# Revit family: 206_HDW-_
name_source: partatom
category: Duct Accessories
units: mm (PartAtom-declared; Revit-internal decimal feet)

## family parameters
Always vertical = Yes
Cut with Voids When Loaded = No
Part Type = Breaks Into
Round Connector Dimension = Use Diameter
Shared = No
Work Plane-Based = No

## types (7) — shared parameters
CAT0 = Yes
Description = HEATING COIL FOR CIRCULAR DUCTING
Manufacturer = Alnor
QmdConnectorList = 201;D;202;D
URL = http://www.ventilation-alnor.co.uk
magiPartTypeId = 206
magiProductFamilyId = HDW-*

## per-type parameters (varying)
| type | CBB | CH | CHH | D | H2D | L2D | LL | W2D |
| HDW-100 | 108 mm | 190 mm  [stored 0.62336 ft] | 95 mm  [stored 0.31168 ft] | 100 mm | 190 mm  [stored 0.62336 ft] | 220 mm  [stored 0.721785 ft] | 110 mm  [stored 0.360892 ft] | 214 mm |
| HDW-315 | 230 mm | 440 mm | 220 mm  [stored 0.721785 ft] | 315 mm | 439 mm | 260 mm | 130 mm | 459 mm |
| HDW-250 | 198 mm | 365 mm | 183 mm | 250 mm | 364 mm | 260 mm | 130 mm | 394 mm |
| HDW-200 | 145 mm | 265 mm | 133 mm | 200 mm | 264 mm | 220 mm  [stored 0.721785 ft] | 110 mm  [stored 0.360892 ft] | 290 mm |
| HDW-160 | 145 mm | 265 mm | 133 mm | 160 mm | 264 mm | 220 mm  [stored 0.721785 ft] | 110 mm  [stored 0.360892 ft] | 290 mm |
| HDW-150 | 145 mm | 265 mm | 133 mm | 150 mm | 264 mm | 220 mm  [stored 0.721785 ft] | 110 mm  [stored 0.360892 ft] | 290 mm |
| HDW-125 | 108 mm | 190 mm  [stored 0.62336 ft] | 95 mm  [stored 0.31168 ft] | 125 mm | 189 mm | 220 mm  [stored 0.721785 ft] | 110 mm  [stored 0.360892 ft] | 215 mm  [stored 0.705381 ft] |

note: column(s) folded — value = type name in every type: MC Product Code, magiProductId

note: [stored X ft] marks values corroborated as IEEE doubles in the binary element streams (Revit-internal decimal feet)

## geometry (parser evidence)
native form markers: Blend x4, Sweep x2
no freeform markers — native parametric forms only
